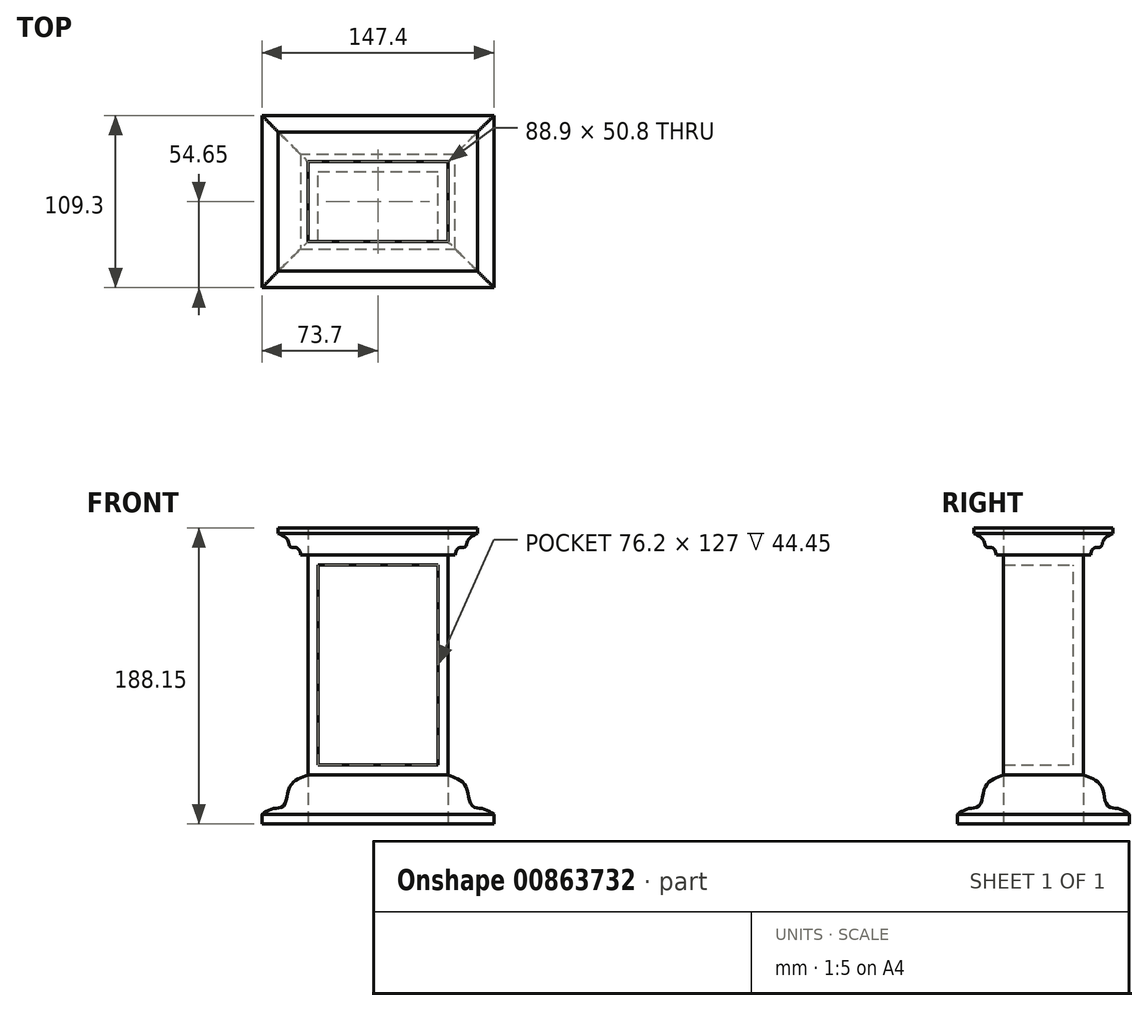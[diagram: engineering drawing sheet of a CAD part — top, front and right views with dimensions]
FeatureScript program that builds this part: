
annotation { "Feature Type Name" : "Feature", "Feature Type Description" : "" }
export const myFeature = defineFeature(function(context is Context, id is Id, definition is map)
    precondition{}
    {
        {
            var Q0;
            Q0=qCreatedBy(makeId("Front.planeOp"),FACE);
            var sketch = newSketch(context, id + "F0", { "sketchPlane" : qUnion([Q0])});
            skLineSegment(sketch, "E0.bottom", {"start": v(0, 0) * mm, "end": v(88.9, 0) * mm});
            skLineSegment(sketch, "E0.top", {"start": v(0, 139.7) * mm, "end": v(88.9, 139.7) * mm});
            skLineSegment(sketch, "E0.left", {"start": v(0, 0) * mm, "end": v(0, 139.7) * mm});
            skLineSegment(sketch, "E0.right", {"start": v(88.9, 0) * mm, "end": v(88.9, 139.7) * mm});
            skSolve(sketch);
        }
        {
            var Q0;
            Q0=makeQuery(id+"F0.imprint","IMPRINT",FACE,{"disambiguationData":[TD([[makeQuery(id+"F0.imprint","IMPRINT",EDGE,{"derivedFrom":sQuery(id+"F0.wireOp",EDGE,"E0.bottom")}),1.0]])]});
            extrude(context, id + "F1", {"entities" : qUnion([Q0]), "depth" : 50.8 * mm, "offsetDistance" : 25.4 * mm});
        }
        {
            var Q0;
            Q0=makeQuery(id+"F1.opExtrude","CAP_FACE",FACE,{"disambiguationData":[OSD([sQuery(id+"F0.wireOp",EDGE,"E0.bottom"),sQuery(id+"F0.wireOp",EDGE,"E0.top"),sQuery(id+"F0.wireOp",EDGE,"E0.left"),sQuery(id+"F0.wireOp",EDGE,"E0.right")])],"isStart":false});
            shell(context, id + "F2", {"entities" : qUnion([Q0]), "thickness" : 6.35 * mm});
        }
        {
            var Q0;
            Q0=makeQuery(id+"F1.opExtrude","SWEPT_FACE",FACE,{"disambiguationData":[OSD([sQuery(id+"F0.wireOp",EDGE,"E0.top")])]});
            var sketch = newSketch(context, id + "F3", { "sketchPlane" : qUnion([Q0])});
            skLineSegment(sketch, "E1", {"start": v(0, 0) * mm, "end": v(0, -50.8) * mm});
            skLineSegment(sketch, "E2", {"start": v(0, -50.8) * mm, "end": v(88.9, -50.8) * mm});
            skLineSegment(sketch, "E3", {"start": v(88.9, -50.8) * mm, "end": v(88.9, 0) * mm});
            skSolve(sketch);
        }
        {
            var Q0;
            Q0=makeQuery(id+"F1.opExtrude","CAP_FACE",FACE,{"disambiguationData":[OSD([sQuery(id+"F0.wireOp",EDGE,"E0.bottom"),sQuery(id+"F0.wireOp",EDGE,"E0.top"),sQuery(id+"F0.wireOp",EDGE,"E0.left"),sQuery(id+"F0.wireOp",EDGE,"E0.right")])],"isStart":true});
            var sketch = newSketch(context, id + "F4", { "sketchPlane" : qUnion([Q0])});
            skLineSegment(sketch, "E4", {"start": v(0, 139.7) * mm, "end": v(0, 157.06) * mm});
            skLineSegment(sketch, "E5", {"start": v(0, 157.06) * mm, "end": v(18.81, 157.06) * mm});
            skLineSegment(sketch, "E6", {"start": v(18.81, 157.06) * mm, "end": v(18.81, 153.38) * mm});
            skLineSegment(sketch, "E7", {"start": v(0, 139.7) * mm, "end": v(4.62, 139.7) * mm});
            skFitSpline(sketch, "E8", {"points": [v(18.81, 153.38) * mm, v(12.54, 148.74) * mm, v(10.76, 144.78) * mm, v(4.62, 139.7) * mm], "startDerivative": vector(-26, -12.06) * mm, "endDerivative": vector(-4.66, -51.57) * mm});
            skSolve(sketch);
        }
        {
            var Q0;
            Q0=makeQuery(id+"F4.imprint","IMPRINT",FACE,{"disambiguationData":[TD([[makeQuery(id+"F4.imprint","IMPRINT",EDGE,{"derivedFrom":sQuery(id+"F4.wireOp",EDGE,"E4")}),-1.0]])]});
            var Q1;
            Q1=sQuery(id+"F3.wireOp",EDGE,"E1");
            var Q2;
            Q2=makeQuery(id+"F1.opExtrude","CAP_EDGE",EDGE,{"disambiguationData":[OSD([sQuery(id+"F0.wireOp",EDGE,"E0.top")])],"isStart":true});
            var Q3;
            Q3=sQuery(id+"F3.wireOp",EDGE,"E2");
            var Q4;
            Q4=sQuery(id+"F3.wireOp",EDGE,"E3");
            sweep(context, id + "F5", {"profiles" : qUnion([Q0]), "path" : qUnion([Q1, Q2, Q3, Q4])});
        }
        {
            var Q0;
            Q0=makeQuery(id+"F1.opExtrude","SWEPT_FACE",FACE,{"disambiguationData":[OSD([sQuery(id+"F0.wireOp",EDGE,"E0.bottom")])]});
            var sketch = newSketch(context, id + "F6", { "sketchPlane" : qUnion([Q0])});
            skLineSegment(sketch, "E9", {"start": v(0, 50.8) * mm, "end": v(0, 0) * mm});
            skLineSegment(sketch, "E10", {"start": v(0, 0) * mm, "end": v(88.9, 0) * mm});
            skLineSegment(sketch, "E11", {"start": v(88.9, 0) * mm, "end": v(88.9, 50.8) * mm});
            skSolve(sketch);
        }
        {
            var Q0;
            Q0=makeQuery(id+"F1.opExtrude","CAP_FACE",FACE,{"disambiguationData":[OSD([sQuery(id+"F0.wireOp",EDGE,"E0.bottom"),sQuery(id+"F0.wireOp",EDGE,"E0.top"),sQuery(id+"F0.wireOp",EDGE,"E0.left"),sQuery(id+"F0.wireOp",EDGE,"E0.right")])],"isStart":true});
            var sketch = newSketch(context, id + "F7", { "sketchPlane" : qUnion([Q0])});
            skLineSegment(sketch, "E12", {"start": v(0, 0) * mm, "end": v(0, -31.09) * mm});
            skLineSegment(sketch, "E13", {"start": v(0, -31.09) * mm, "end": v(29.25, -31.09) * mm});
            skLineSegment(sketch, "E14", {"start": v(29.25, -31.09) * mm, "end": v(29.25, -25.14) * mm});
            skFitSpline(sketch, "E15", {"points": [v(29.25, -25.14) * mm, v(22.31, -21.42) * mm, v(15.12, -19.19) * mm, v(11.4, -7.29) * mm, v(0, 0) * mm], "startDerivative": vector(-29.4, 21) * mm, "endDerivative": vector(-48.41, 17.6) * mm});
            skSolve(sketch);
        }
        {
            var Q0;
            Q0=makeQuery(id+"F7.imprint","IMPRINT",FACE,{"disambiguationData":[TD([[makeQuery(id+"F7.imprint","IMPRINT",EDGE,{"derivedFrom":sQuery(id+"F7.wireOp",EDGE,"E12")}),1.0]])]});
            var Q1;
            Q1=sQuery(id+"F6.wireOp",EDGE,"E9");
            var Q2;
            Q2=makeQuery(id+"F1.opExtrude","CAP_EDGE",EDGE,{"disambiguationData":[OSD([sQuery(id+"F0.wireOp",EDGE,"E0.bottom")])],"isStart":false});
            var Q3;
            Q3=sQuery(id+"F6.wireOp",EDGE,"E10");
            var Q4;
            Q4=sQuery(id+"F6.wireOp",EDGE,"E11");
            sweep(context, id + "F8", {"profiles" : qUnion([Q0]), "path" : qUnion([Q1, Q2, Q3, Q4])});
        }
    });
